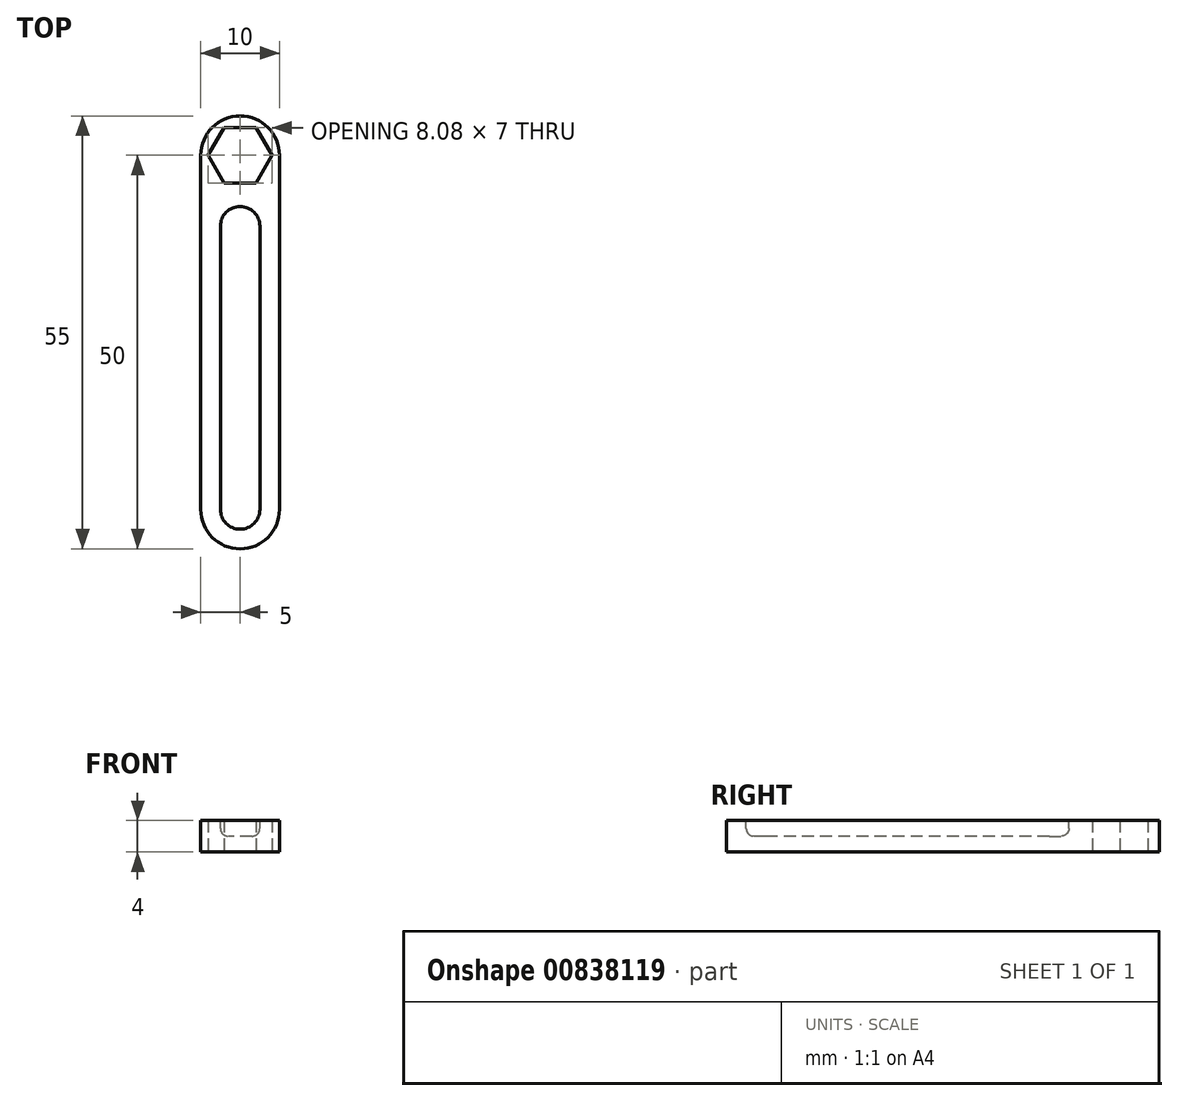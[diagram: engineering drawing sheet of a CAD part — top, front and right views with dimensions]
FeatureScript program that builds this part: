
annotation { "Feature Type Name" : "Feature", "Feature Type Description" : "" }
export const myFeature = defineFeature(function(context is Context, id is Id, definition is map)
    precondition{}
    {
        {
            var Q0;
            Q0=qCreatedBy(makeId("Top.planeOp"),FACE);
            var sketch = newSketch(context, id + "F0", { "sketchPlane" : qUnion([Q0])});
            skCircle(sketch, "E0.cCircle", {"center": v(0, 0) * mm, "radius": 3.5 * mm, "construction": true});
            skLineSegment(sketch, "E0.0", {"start": v(-2.02, 3.5) * mm, "end": v(2.02, 3.5) * mm});
            skLineSegment(sketch, "E0.1", {"start": v(2.02, 3.5) * mm, "end": v(4.04, 0) * mm});
            skLineSegment(sketch, "E0.2", {"start": v(4.04, 0) * mm, "end": v(2.02, -3.5) * mm});
            skLineSegment(sketch, "E0.3", {"start": v(2.02, -3.5) * mm, "end": v(-2.02, -3.5) * mm});
            skLineSegment(sketch, "E0.4", {"start": v(-2.02, -3.5) * mm, "end": v(-4.04, 0) * mm});
            skLineSegment(sketch, "E0.5", {"start": v(-4.04, 0) * mm, "end": v(-2.02, 3.5) * mm});
            skPoint(sketch, "E0.0.midPoint", {"position": v(0, 3.5) * mm});
            skCircle(sketch, "E1", {"center": v(0, 0) * mm, "radius": 5 * mm});
            skArc(sketch, "E2", {"start": v(-5, -45) * mm, "mid": v(0, -50) * mm, "end": v(5, -45) * mm});
            skLineSegment(sketch, "E3", {"start": v(5, -45) * mm, "end": v(5, 0) * mm});
            skLineSegment(sketch, "E4", {"start": v(-5, 0) * mm, "end": v(-5, -45) * mm});
            skSolve(sketch);
        }
        {
            var Q0;
            Q0 = qSketchRegion(id + "F0", true);
            extrude(context, id + "F1", {"entities" : qUnion([Q0]), "depth" : 4 * mm, "offsetDistance" : 25 * mm});
        }
        {
            var Q0;
            Q0=makeQuery(id+"F1.opExtrude","CAP_FACE",FACE,{"disambiguationData":[OSD([sQuery(id+"F0.wireOp",EDGE,"E0.0"),sQuery(id+"F0.wireOp",EDGE,"E0.1"),sQuery(id+"F0.wireOp",EDGE,"E0.2"),sQuery(id+"F0.wireOp",EDGE,"E0.3"),sQuery(id+"F0.wireOp",EDGE,"E0.4"),sQuery(id+"F0.wireOp",EDGE,"E0.5"),sQuery(id+"F0.wireOp",EDGE,"E1"),sQuery(id+"F0.wireOp",EDGE,"E2"),sQuery(id+"F0.wireOp",EDGE,"E3"),sQuery(id+"F0.wireOp",EDGE,"E4")])],"isStart":false});
            var sketch = newSketch(context, id + "F2", { "sketchPlane" : qUnion([Q0])});
            skLineSegment(sketch, "E5.left", {"start": v(-2.5, -9) * mm, "end": v(-2.5, -45) * mm});
            skLineSegment(sketch, "E5.right", {"start": v(2.5, -9) * mm, "end": v(2.5, -45) * mm});
            skPoint(sketch, "E5.middle", {"position": v(0, -27) * mm});
            skArc(sketch, "E6", {"start": v(2.5, -9) * mm, "mid": v(0, -6.5) * mm, "end": v(-2.5, -9) * mm});
            skPoint(sketch, "E6.third.point", {"position": v(0, -6.5) * mm});
            skPoint(sketch, "E6.third.point.positionSnap0", {"position": v(0, -9) * mm});
            skArc(sketch, "E7", {"start": v(-2.5, -45) * mm, "mid": v(0, -47.5) * mm, "end": v(2.5, -45) * mm});
            skPoint(sketch, "E7.third.point", {"position": v(0, -47.5) * mm});
            skPoint(sketch, "E7.third.point.positionSnap0", {"position": v(0, -45) * mm});
            skSolve(sketch);
        }
        {
            var Q0;
            Q0=makeQuery(id+"F2.imprint","IMPRINT",FACE,{"disambiguationData":[TD([[makeQuery(id+"F2.imprint","IMPRINT",EDGE,{"derivedFrom":sQuery(id+"F2.wireOp",EDGE,"E5.left")}),1.0]])]});
            extrude(context, id + "F3", {"entities" : qUnion([Q0]), "operationType" : NewBodyOperationType.REMOVE, "oppositeDirection" : true, "depth" : 2 * mm, "offsetDistance" : 25 * mm});
        }
        {
            var Q0;
            Q0=makeQuery(id+"F3.boolean.opBoolean","COPY",FACE,{"derivedFrom":makeQuery(id+"F3.opExtrude","CAP_FACE",FACE,{"disambiguationData":[OSD([sQuery(id+"F2.wireOp",EDGE,"E5.left"),sQuery(id+"F2.wireOp",EDGE,"E5.right"),sQuery(id+"F2.wireOp",EDGE,"E6"),sQuery(id+"F2.wireOp",EDGE,"E7")])],"isStart":false})});
            fillet(context, id + "F4", {"entities" : qUnion([Q0]), "radius" : 1 * mm, "tangentPropagation" : true, "allowEdgeOverflow" : false});
        }
    });
